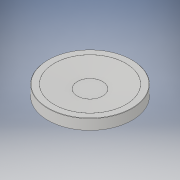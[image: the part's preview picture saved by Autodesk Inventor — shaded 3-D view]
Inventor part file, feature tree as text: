
AUTODESK INVENTOR PART (.ipt)
format: ipt  version: 2019.4 (Build 234330000, 330)  size: 126,464 bytes
history: native  units: mm
features: fillet x3, other x1, revolve x1, sketch x1
ambient origin geometry x8: Origin, YZ Plane, XZ Plane, XY Plane, X Axis, Y Axis, Z Axis, Center Point
bodies: Body1 (feature_tree)
feature tree (6):
  other  "Sólido1"
  revolve  "Revolución1"  [1 undecoded]
  fillet  "Empalme1"  Radius=300.0mm
  fillet  "Empalme2"  Radius=1200.0mm
  fillet  "Empalme3"  Radius=300.0mm
  sketch  "Boceto1"  dims[d0=1000.0mm d1=4000.0mm d2=300.0mm d4=1200.0mm d5=300.0mm d6=90.0deg d7=30.0mm d8=30.0mm d9=30.0mm]
note: 1 required parameter value undecoded (feature->parameter linkage not recoverable at this tier; creation-order binding heuristic only, values carry confidence <= 0.55)
